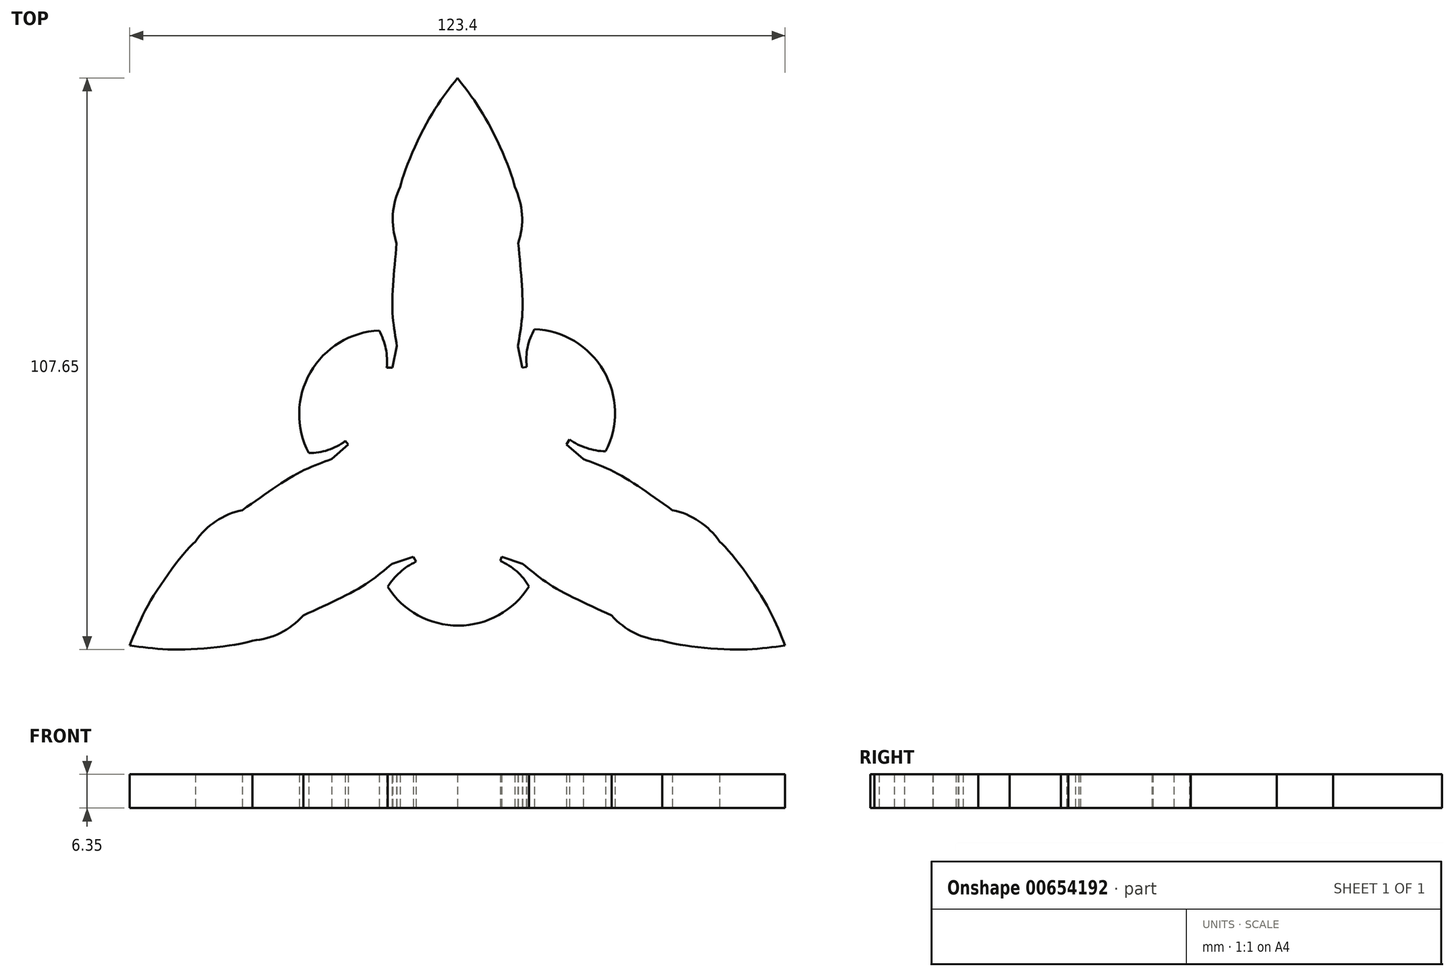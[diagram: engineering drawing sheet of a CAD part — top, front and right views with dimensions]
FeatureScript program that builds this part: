
annotation { "Feature Type Name" : "Feature", "Feature Type Description" : "" }
export const myFeature = defineFeature(function(context is Context, id is Id, definition is map)
    precondition{}
    {
        {
            var Q0;
            Q0=qCreatedBy(makeId("Top.planeOp"),FACE);
            var sketch = newSketch(context, id + "F0", { "sketchPlane" : qUnion([Q0])});
            skArc(sketch, "E0", {"start": v(-10.77, 50.76) * mm, "mid": v(-12.15, 45.52) * mm, "end": v(-11.46, 40.14) * mm});
            skFitSpline(sketch, "E1", {"points": [v(0, 71.24) * mm, v(-5.72, 62.89) * mm, v(-10.77, 50.76) * mm, v(-10.77, 48.82) * mm], "startDerivative": vector(-14.47, -18.62) * mm, "endDerivative": vector(1.7, -8.93) * mm});
            skLineSegment(sketch, "E2", {"start": v(-12.22, 16.67) * mm, "end": v(-11.4, 20.76) * mm});
            skFitSpline(sketch, "E3", {"points": [v(-11.4, 20.76) * mm, v(-12.25, 27.64) * mm, v(-11.46, 40.14) * mm], "startDerivative": vector(-2.34, 15.12) * mm, "endDerivative": vector(1.99, 23.38) * mm});
            skFitSpline(sketch, "E4.MirrorCS", {"points": [v(0, 71.24) * mm, v(5.72, 62.89) * mm, v(10.77, 50.76) * mm, v(10.77, 48.82) * mm], "startDerivative": vector(14.47, -18.62) * mm, "endDerivative": vector(-1.7, -8.93) * mm});
            skArc(sketch, "E5.MirrorCS", {"start": v(10.77, 50.76) * mm, "mid": v(12.15, 45.52) * mm, "end": v(11.46, 40.14) * mm});
            skFitSpline(sketch, "E6.MirrorCS", {"points": [v(11.4, 20.76) * mm, v(12.25, 27.64) * mm, v(11.46, 40.14) * mm], "startDerivative": vector(2.34, 15.12) * mm, "endDerivative": vector(-1.99, 23.38) * mm});
            skPoint(sketch, "E7.center", {"position": v(0, 0) * mm});
            skLineSegment(sketch, "E8", {"start": v(-20.54, 2.25) * mm, "end": v(-21.1, 2.89) * mm});
            skLineSegment(sketch, "E9", {"start": v(-12.22, 16.67) * mm, "end": v(-13.3, 16.67) * mm});
            skArc(sketch, "E10", {"start": v(-27.98, 0.6) * mm, "mid": v(-24.36, 1.17) * mm, "end": v(-21.1, 2.89) * mm});
            skArc(sketch, "E11", {"start": v(-13.3, 16.67) * mm, "mid": v(-13.5, 20.28) * mm, "end": v(-14.74, 23.68) * mm});
            skArc(sketch, "E12", {"start": v(-14.74, 23.68) * mm, "mid": v(-27.7, 15.79) * mm, "end": v(-27.98, 0.6) * mm});
            skPoint(sketch, "E13.center", {"position": v(-0.15, 0.15) * mm});
            skLineSegment(sketch, "E14", {"start": v(-20.54, 2.25) * mm, "end": v(-12.22, 16.67) * mm});
            skPoint(sketch, "E15.1.1", {"position": v(-0.05, -0.2) * mm});
            skArc(sketch, "E15.1.2", {"start": v(-13.14, -24.6) * mm, "mid": v(0.18, -31.89) * mm, "end": v(13.47, -24.54) * mm});
            skLineSegment(sketch, "E15.1.4", {"start": v(8.33, -18.91) * mm, "end": v(-8.33, -18.91) * mm});
            skArc(sketch, "E15.1.7", {"start": v(13.47, -24.54) * mm, "mid": v(11.16, -21.68) * mm, "end": v(8.05, -19.72) * mm});
            skLineSegment(sketch, "E15.1.8", {"start": v(8.33, -18.91) * mm, "end": v(8.05, -19.72) * mm});
            skArc(sketch, "E15.1.10", {"start": v(-7.79, -19.85) * mm, "mid": v(-10.81, -21.83) * mm, "end": v(-13.14, -24.6) * mm});
            skLineSegment(sketch, "E15.1.11", {"start": v(-8.33, -18.91) * mm, "end": v(-7.79, -19.85) * mm});
            skPoint(sketch, "E15.2.1", {"position": v(0.2, 0.06) * mm});
            skArc(sketch, "E15.2.2", {"start": v(27.88, 0.92) * mm, "mid": v(27.52, 16.1) * mm, "end": v(14.52, 23.93) * mm});
            skLineSegment(sketch, "E15.2.4", {"start": v(12.22, 16.67) * mm, "end": v(20.54, 2.25) * mm});
            skArc(sketch, "E15.2.7", {"start": v(14.52, 23.93) * mm, "mid": v(13.2, 20.5) * mm, "end": v(13.05, 16.84) * mm});
            skLineSegment(sketch, "E15.2.8", {"start": v(12.22, 16.67) * mm, "end": v(13.05, 16.84) * mm});
            skArc(sketch, "E15.2.10", {"start": v(21.08, 3.18) * mm, "mid": v(24.31, 1.55) * mm, "end": v(27.88, 0.92) * mm});
            skLineSegment(sketch, "E15.2.11", {"start": v(20.54, 2.25) * mm, "end": v(21.08, 3.18) * mm});
            skLineSegment(sketch, "E16", {"start": v(11.4, 20.76) * mm, "end": v(12.22, 16.67) * mm});
            skArc(sketch, "E17", {"start": v(-38.57, -34.71) * mm, "mid": v(-33.34, -33.28) * mm, "end": v(-29.03, -30) * mm});
            skFitSpline(sketch, "E18", {"points": [v(-61.7, -35.62) * mm, v(-51.6, -36.4) * mm, v(-38.57, -34.71) * mm, v(-36.9, -33.74) * mm], "startDerivative": vector(23.36, -3.22) * mm, "endDerivative": vector(6.88, 5.93) * mm});
            skLineSegment(sketch, "E19", {"start": v(-8.33, -18.91) * mm, "end": v(-12.28, -20.25) * mm});
            skFitSpline(sketch, "E20", {"points": [v(-12.28, -20.25) * mm, v(-17.81, -24.43) * mm, v(-29.03, -30) * mm], "startDerivative": vector(-11.92, -9.6) * mm, "endDerivative": vector(-21.24, -9.97) * mm});
            skFitSpline(sketch, "E21.MirrorCS", {"points": [v(-61.7, -35.62) * mm, v(-57.32, -26.49) * mm, v(-49.35, -16.05) * mm, v(-47.67, -15.08) * mm], "startDerivative": vector(8.9, 21.84) * mm, "endDerivative": vector(8.58, 3) * mm});
            skArc(sketch, "E22.MirrorCS", {"start": v(-49.35, -16.05) * mm, "mid": v(-45.5, -12.23) * mm, "end": v(-40.49, -10.15) * mm});
            skFitSpline(sketch, "E23.MirrorCS", {"points": [v(-23.68, -0.5) * mm, v(-30.06, -3.2) * mm, v(-40.49, -10.15) * mm], "startDerivative": vector(-14.27, -5.53) * mm, "endDerivative": vector(-19.25, -13.4) * mm});
            skLineSegment(sketch, "E24", {"start": v(-23.68, -0.5) * mm, "end": v(-20.54, 2.25) * mm});
            skLineSegment(sketch, "E25", {"start": v(-8.33, -18.91) * mm, "end": v(-20.54, 2.25) * mm});
            skLineSegment(sketch, "E26", {"start": v(20.54, 2.25) * mm, "end": v(8.33, -18.91) * mm});
            skArc(sketch, "E27", {"start": v(49.35, -16.05) * mm, "mid": v(45.5, -12.23) * mm, "end": v(40.49, -10.15) * mm});
            skFitSpline(sketch, "E28", {"points": [v(61.7, -35.62) * mm, v(57.32, -26.49) * mm, v(49.35, -16.05) * mm, v(47.67, -15.08) * mm], "startDerivative": vector(-8.9, 21.84) * mm, "endDerivative": vector(-8.58, 3) * mm});
            skLineSegment(sketch, "E29", {"start": v(20.54, 2.25) * mm, "end": v(23.68, -0.5) * mm});
            skFitSpline(sketch, "E30", {"points": [v(23.68, -0.5) * mm, v(30.06, -3.2) * mm, v(40.49, -10.15) * mm], "startDerivative": vector(14.27, -5.53) * mm, "endDerivative": vector(19.25, -13.4) * mm});
            skFitSpline(sketch, "E31.MirrorCS", {"points": [v(61.7, -35.62) * mm, v(51.6, -36.4) * mm, v(38.57, -34.71) * mm, v(36.9, -33.74) * mm], "startDerivative": vector(-23.36, -3.22) * mm, "endDerivative": vector(-6.88, 5.93) * mm});
            skArc(sketch, "E32.MirrorCS", {"start": v(38.57, -34.71) * mm, "mid": v(33.34, -33.28) * mm, "end": v(29.03, -30) * mm});
            skFitSpline(sketch, "E33.MirrorCS", {"points": [v(12.28, -20.25) * mm, v(17.81, -24.43) * mm, v(29.03, -30) * mm], "startDerivative": vector(11.92, -9.6) * mm, "endDerivative": vector(21.24, -9.97) * mm});
            skLineSegment(sketch, "E34", {"start": v(12.28, -20.25) * mm, "end": v(8.33, -18.91) * mm});
            skSolve(sketch);
        }
        {
            var Q0;
            Q0=makeQuery(id+"F0.imprint","IMPRINT",FACE,{"disambiguationData":[TD([[makeQuery(id+"F0.imprint","IMPRINT",EDGE,{"derivedFrom":sQuery(id+"F0.wireOp",EDGE,"E0")}),1.0]])]});
            var Q1;
            Q1=makeQuery(id+"F0.imprint","IMPRINT",FACE,{"disambiguationData":[TD([[makeQuery(id+"F0.imprint","IMPRINT",EDGE,{"derivedFrom":sQuery(id+"F0.wireOp",EDGE,"E8")}),-1.0]])]});
            var Q2;
            Q2=makeQuery(id+"F0.imprint","IMPRINT",FACE,{"disambiguationData":[TD([[makeQuery(id+"F0.imprint","IMPRINT",EDGE,{"derivedFrom":sQuery(id+"F0.wireOp",EDGE,"E17")}),1.0]])]});
            var Q3;
            Q3=makeQuery(id+"F0.imprint","IMPRINT",FACE,{"disambiguationData":[TD([[makeQuery(id+"F0.imprint","IMPRINT",EDGE,{"derivedFrom":sQuery(id+"F0.wireOp",EDGE,"E15.1.2")}),1.0]])]});
            var Q4;
            Q4=makeQuery(id+"F0.imprint","IMPRINT",FACE,{"disambiguationData":[TD([[makeQuery(id+"F0.imprint","IMPRINT",EDGE,{"derivedFrom":sQuery(id+"F0.wireOp",EDGE,"E26")}),1.0]])]});
            var Q5;
            Q5=makeQuery(id+"F0.imprint","IMPRINT",FACE,{"disambiguationData":[TD([[makeQuery(id+"F0.imprint","IMPRINT",EDGE,{"derivedFrom":sQuery(id+"F0.wireOp",EDGE,"E15.2.2")}),1.0]])]});
            extrude(context, id + "F1", {"entities" : qUnion([Q0, Q1, Q2, Q3, Q4, Q5]), "depth" : 6.35 * mm, "offsetDistance" : 25.4 * mm});
        }
    });
